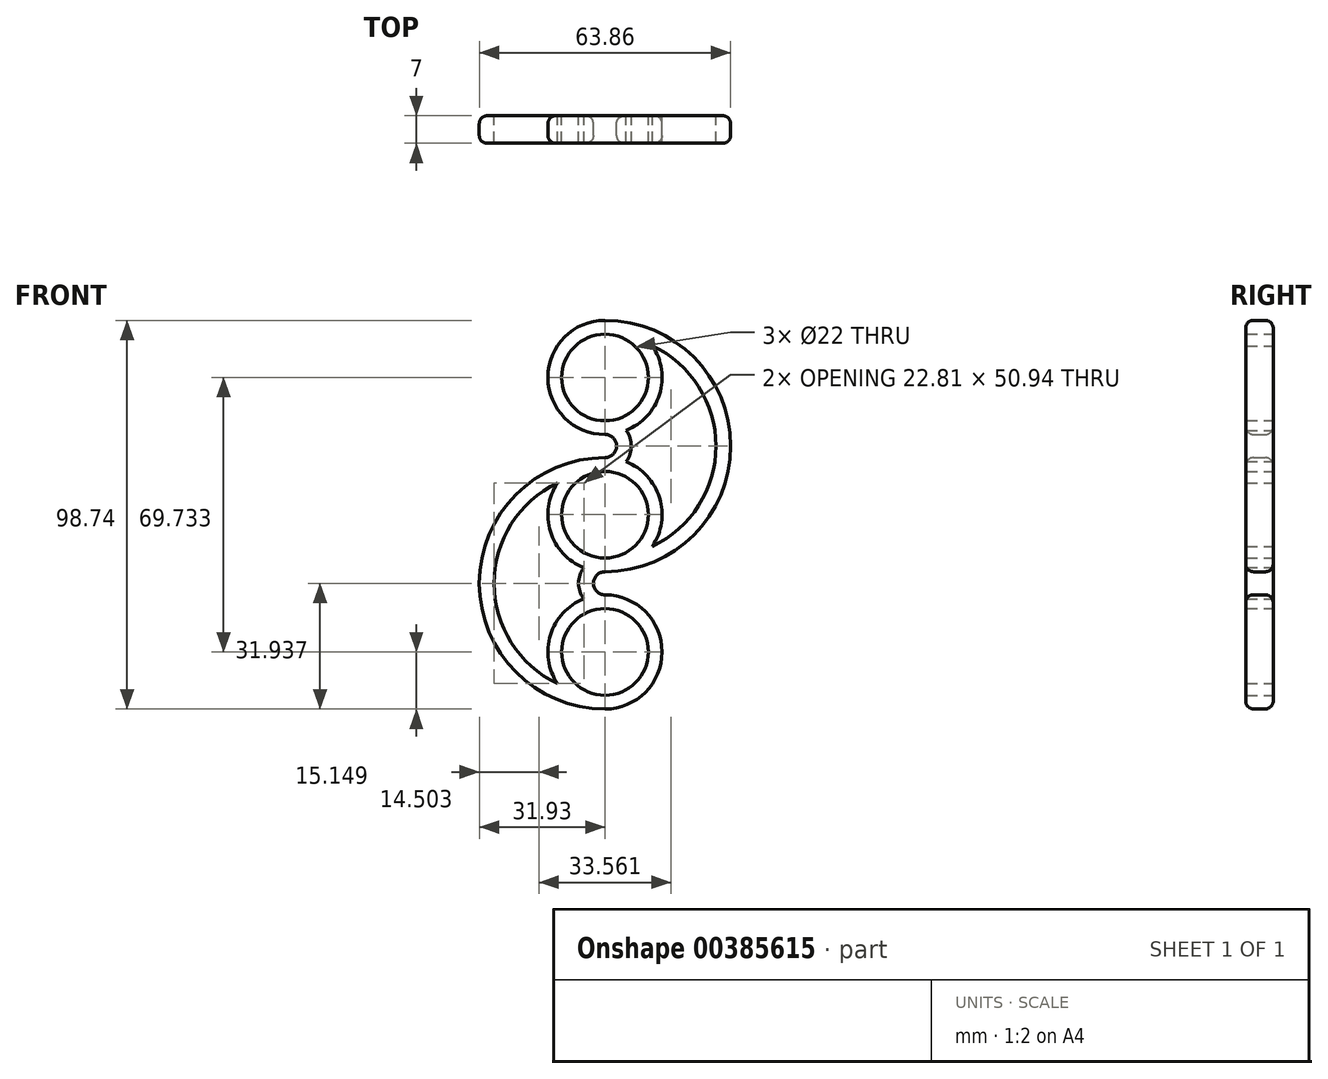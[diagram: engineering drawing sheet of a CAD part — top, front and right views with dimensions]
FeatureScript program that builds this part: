
annotation { "Feature Type Name" : "Feature", "Feature Type Description" : "" }
export const myFeature = defineFeature(function(context is Context, id is Id, definition is map)
    precondition{}
    {
        {
            var Q0;
            Q0=qCreatedBy(makeId("Front.planeOp"),FACE);
            var sketch = newSketch(context, id + "F0", { "sketchPlane" : qUnion([Q0])});
            skArc(sketch, "E0", {"start": v(12.07, -8.03) * mm, "mid": v(13.84, 4.3) * mm, "end": v(5.38, 13.47) * mm});
            skCircle(sketch, "E1", {"center": v(0, 0) * mm, "radius": 11 * mm});
            skArc(sketch, "E2", {"start": v(0, 49.37) * mm, "mid": v(-14.5, 34.87) * mm, "end": v(0, 20.37) * mm});
            skCircle(sketch, "E3", {"center": v(0, 34.87) * mm, "radius": 11 * mm});
            skArc(sketch, "E4", {"start": v(0, 14.5) * mm, "mid": v(2.93, 17.43) * mm, "end": v(0, 20.37) * mm});
            skArc(sketch, "E5.0", {"start": v(5.38, 13.47) * mm, "mid": v(6.68, 17.43) * mm, "end": v(5.38, 21.4) * mm});
            skArc(sketch, "E6", {"start": v(0, -14.5) * mm, "mid": v(31.93, 17.43) * mm, "end": v(0, 49.37) * mm});
            skArc(sketch, "E7.0", {"start": v(12.07, -8.03) * mm, "mid": v(28.18, 17.43) * mm, "end": v(12.07, 42.9) * mm});
            skArc(sketch, "E8.trimOffspring", {"start": v(5.38, 21.4) * mm, "mid": v(13.84, 30.56) * mm, "end": v(12.07, 42.9) * mm});
            skArc(sketch, "E9.trimOffspring", {"start": v(-12.07, 8.03) * mm, "mid": v(-13.84, -4.3) * mm, "end": v(-5.38, -13.47) * mm});
            skArc(sketch, "E10.1.0", {"start": v(0, -49.37) * mm, "mid": v(14.5, -34.87) * mm, "end": v(0, -20.37) * mm});
            skArc(sketch, "E10.1.1", {"start": v(0, 14.5) * mm, "mid": v(-31.93, -17.43) * mm, "end": v(0, -49.37) * mm});
            skCircle(sketch, "E10.1.2", {"center": v(0, -34.87) * mm, "radius": 11 * mm});
            skArc(sketch, "E10.1.3", {"start": v(-12.07, 8.03) * mm, "mid": v(-28.18, -17.43) * mm, "end": v(-12.07, -42.9) * mm});
            skArc(sketch, "E10.1.4", {"start": v(-5.38, -21.4) * mm, "mid": v(-13.84, -30.56) * mm, "end": v(-12.07, -42.9) * mm});
            skArc(sketch, "E10.1.5", {"start": v(-5.38, -13.47) * mm, "mid": v(-6.68, -17.43) * mm, "end": v(-5.38, -21.4) * mm});
            skArc(sketch, "E10.1.6", {"start": v(0, -14.5) * mm, "mid": v(-2.93, -17.43) * mm, "end": v(0, -20.37) * mm});
            skSolve(sketch);
        }
        {
            var Q0;
            Q0=makeQuery(id+"F0.imprint","IMPRINT",FACE,{"disambiguationData":[TD([[makeQuery(id+"F0.imprint","IMPRINT",EDGE,{"derivedFrom":sQuery(id+"F0.wireOp",EDGE,"E0")}),1.0]])]});
            extrude(context, id + "F1", {"entities" : qUnion([Q0]), "depth" : 7 * mm});
        }
        {
            var Q0;
            Q0=makeQuery(id+"F1.opExtrude","CAP_EDGE",EDGE,{"disambiguationData":[OSD([sQuery(id+"F0.wireOp",EDGE,"E10.1.1")])],"isStart":false});
            var Q1;
            Q1=makeQuery(id+"F1.opExtrude","CAP_EDGE",EDGE,{"disambiguationData":[OSD([sQuery(id+"F0.wireOp",EDGE,"E10.1.1")])],"isStart":true});
            fillet(context, id + "F2", {"entities" : qUnion([Q0, Q1]), "radius" : 2 * mm, "tangentPropagation" : true, "allowEdgeOverflow" : false});
        }
    });
